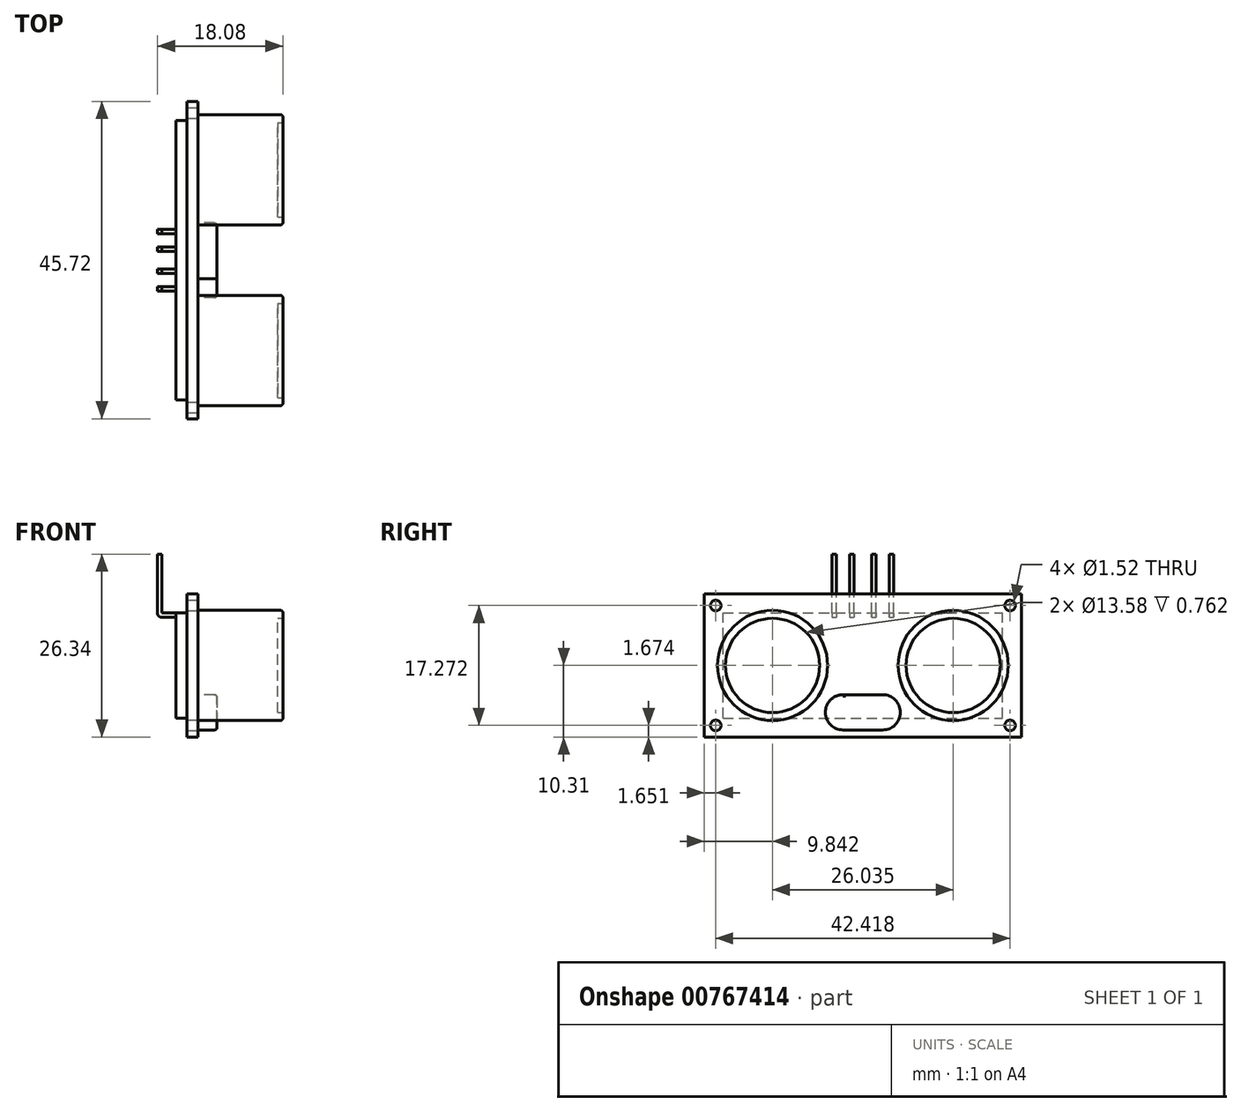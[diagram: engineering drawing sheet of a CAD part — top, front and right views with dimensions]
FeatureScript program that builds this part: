
annotation { "Feature Type Name" : "Feature", "Feature Type Description" : "" }
export const myFeature = defineFeature(function(context is Context, id is Id, definition is map)
    precondition{}
    {
        {
            var Q0;
            Q0=qCreatedBy(makeId("Right.planeOp"),FACE);
            var sketch = newSketch(context, id + "F0", { "sketchPlane" : qUnion([Q0])});
            skLineSegment(sketch, "E0.bottom", {"start": v(22.86, -10.31) * mm, "end": v(-22.86, -10.31) * mm});
            skLineSegment(sketch, "E0.top", {"start": v(22.86, 10.31) * mm, "end": v(-22.86, 10.31) * mm});
            skLineSegment(sketch, "E0.left", {"start": v(22.86, -10.31) * mm, "end": v(22.86, 10.31) * mm});
            skLineSegment(sketch, "E0.right", {"start": v(-22.86, -10.31) * mm, "end": v(-22.86, 10.31) * mm});
            skPoint(sketch, "E0.middle", {"position": v(0, 0) * mm});
            skSolve(sketch);
        }
        {
            var Q0;
            Q0=makeQuery(id+"F0.imprint","IMPRINT",FACE,{"disambiguationData":[TD([[makeQuery(id+"F0.imprint","IMPRINT",EDGE,{"derivedFrom":sQuery(id+"F0.wireOp",EDGE,"E0.bottom")}),-1.0]])]});
            extrude(context, id + "F1", {"entities" : qUnion([Q0]), "oppositeDirection" : true, "depth" : 3.17 * mm});
        }
        {
            var Q0;
            Q0=makeQuery(id+"F1.opExtrude","CAP_FACE",FACE,{"disambiguationData":[OSD([sQuery(id+"F0.wireOp",EDGE,"E0.bottom"),sQuery(id+"F0.wireOp",EDGE,"E0.top"),sQuery(id+"F0.wireOp",EDGE,"E0.left"),sQuery(id+"F0.wireOp",EDGE,"E0.right")])],"isStart":true});
            var sketch = newSketch(context, id + "F2", { "sketchPlane" : qUnion([Q0])});
            skLineSegment(sketch, "E1", {"start": v(0, 0) * mm, "end": v(19.75, 0) * mm, "construction": true});
            skLineSegment(sketch, "E2", {"start": v(0, 0) * mm, "end": v(0, -13.51) * mm, "construction": true});
            skCircle(sketch, "E3", {"center": v(-13.02, 0) * mm, "radius": 7.94 * mm});
            skCircle(sketch, "E4.MirrorC", {"center": v(13.02, 0) * mm, "radius": 7.94 * mm});
            skSolve(sketch);
        }
        {
            var Q0;
            Q0=qSketchRegion(id+"F2",true);
            extrude(context, id + "F3", {"entities" : qUnion([Q0]), "operationType" : NewBodyOperationType.ADD, "depth" : 12.24 * mm});
        }
        {
            var Q0;
            Q0=makeQuery(id+"F1.opExtrude","CAP_FACE",FACE,{"disambiguationData":[OSD([sQuery(id+"F0.wireOp",EDGE,"E0.bottom"),sQuery(id+"F0.wireOp",EDGE,"E0.top"),sQuery(id+"F0.wireOp",EDGE,"E0.left"),sQuery(id+"F0.wireOp",EDGE,"E0.right")])],"isStart":true});
            var sketch = newSketch(context, id + "F4", { "sketchPlane" : qUnion([Q0])});
            skLineSegment(sketch, "E5", {"start": v(0, 0) * mm, "end": v(0, -8.96) * mm, "construction": true});
            skLineSegment(sketch, "E6", {"start": v(0, 0) * mm, "end": v(11, 0) * mm, "construction": true});
            skCircle(sketch, "E7", {"center": v(-21.2, 8.64) * mm, "radius": 0.76 * mm});
            skCircle(sketch, "E8.MirrorC", {"center": v(21.2, 8.64) * mm, "radius": 0.76 * mm});
            skCircle(sketch, "E9.MirrorC", {"center": v(-21.2, -8.64) * mm, "radius": 0.76 * mm});
            skCircle(sketch, "E10.MirrorC", {"center": v(21.2, -8.64) * mm, "radius": 0.76 * mm});
            skSolve(sketch);
        }
        {
            var Q0;
            Q0=qSketchRegion(id+"F4",true);
            extrude(context, id + "F5", {"entities" : qUnion([Q0]), "operationType" : NewBodyOperationType.REMOVE, "oppositeDirection" : true, "depth" : 25.4 * mm});
        }
        {
            var Q0;
            Q0=makeQuery(id+"F1.opExtrude","CAP_FACE",FACE,{"disambiguationData":[OSD([sQuery(id+"F0.wireOp",EDGE,"E0.bottom"),sQuery(id+"F0.wireOp",EDGE,"E0.top"),sQuery(id+"F0.wireOp",EDGE,"E0.left"),sQuery(id+"F0.wireOp",EDGE,"E0.right")])],"isStart":false});
            var sketch = newSketch(context, id + "F6", { "sketchPlane" : qUnion([Q0])});
            skLineSegment(sketch, "E11.bottom", {"start": v(20.15, -7.6) * mm, "end": v(-20.15, -7.6) * mm});
            skLineSegment(sketch, "E11.top", {"start": v(20.15, 7.6) * mm, "end": v(-20.15, 7.6) * mm});
            skLineSegment(sketch, "E11.left", {"start": v(20.15, -7.6) * mm, "end": v(20.15, 7.6) * mm});
            skLineSegment(sketch, "E11.right", {"start": v(-20.15, -7.6) * mm, "end": v(-20.15, 7.6) * mm});
            skPoint(sketch, "E11.middle", {"position": v(0, 0) * mm});
            skLineSegment(sketch, "E12.bottom", {"start": v(25.66, -12.83) * mm, "end": v(-25.66, -12.83) * mm});
            skLineSegment(sketch, "E12.top", {"start": v(25.66, 12.83) * mm, "end": v(-25.66, 12.83) * mm});
            skLineSegment(sketch, "E12.left", {"start": v(25.66, -12.83) * mm, "end": v(25.66, 12.83) * mm});
            skLineSegment(sketch, "E12.right", {"start": v(-25.66, -12.83) * mm, "end": v(-25.66, 12.83) * mm});
            skSolve(sketch);
        }
        {
            var Q0;
            Q0=makeQuery(id+"F6.imprint","IMPRINT",FACE,{"disambiguationData":[TD([[makeQuery(id+"F6.imprint","IMPRINT",EDGE,{"derivedFrom":sQuery(id+"F6.wireOp",EDGE,"E11.bottom")}),1.0]])]});
            var Q1;
            Q1=makeQuery(id+"F6.imprint","IMPRINT",FACE,{"disambiguationData":[TD([[makeQuery(id+"F6.imprint","IMPRINT",EDGE,{"derivedFrom":sQuery(id+"F6.wireOp",EDGE,"E12.bottom")}),-1.0]])]});
            extrude(context, id + "F7", {"entities" : qUnion([Q0, Q1]), "operationType" : NewBodyOperationType.REMOVE, "oppositeDirection" : true, "depth" : 1.57 * mm});
        }
        {
            var Q0;
            Q0=makeQuery(id+"F1.opExtrude","CAP_FACE",FACE,{"disambiguationData":[OSD([sQuery(id+"F0.wireOp",EDGE,"E0.bottom"),sQuery(id+"F0.wireOp",EDGE,"E0.top"),sQuery(id+"F0.wireOp",EDGE,"E0.left"),sQuery(id+"F0.wireOp",EDGE,"E0.right")])],"isStart":true});
            var sketch = newSketch(context, id + "F8", { "sketchPlane" : qUnion([Q0])});
            skLineSegment(sketch, "E13.bottom", {"start": v(-2.69, -4.22) * mm, "end": v(2.86, -4.22) * mm});
            skLineSegment(sketch, "E13.top", {"start": v(-2.85, -9.3) * mm, "end": v(2.88, -9.3) * mm});
            skLineSegment(sketch, "E13.left", {"start": v(-5.4, -6.75) * mm, "end": v(-5.4, -6.76) * mm});
            skPoint(sketch, "E13.middle", {"position": v(0, -6.76) * mm});
            skPoint(sketch, "E14.first.point", {"position": v(2.88, -9.3) * mm});
            skPoint(sketch, "E14.second.point", {"position": v(5.4, -6.76) * mm});
            skPoint(sketch, "E14.third.point", {"position": v(3.38, -4.22) * mm});
            skArc(sketch, "E15", {"start": v(-2.69, -4.22) * mm, "mid": v(-5.4, -6.67) * mm, "end": v(-2.85, -9.3) * mm});
            skPoint(sketch, "E15.first.point", {"position": v(-2.85, -9.3) * mm});
            skPoint(sketch, "E15.second.point", {"position": v(-5.4, -6.76) * mm});
            skPoint(sketch, "E15.third.point", {"position": v(-2.69, -4.22) * mm});
            skArc(sketch, "E16", {"start": v(2.86, -9.3) * mm, "mid": v(5.4, -6.76) * mm, "end": v(2.86, -4.22) * mm});
            skPoint(sketch, "E16.first.point", {"position": v(2.86, -9.3) * mm});
            skPoint(sketch, "E16.second.point", {"position": v(2.86, -4.22) * mm});
            skPoint(sketch, "E17.first.point", {"position": v(3.53, -9.3) * mm});
            skPoint(sketch, "E17.second.point", {"position": v(5.4, -5.54) * mm});
            skPoint(sketch, "E17.third.point", {"position": v(4.54, -4.22) * mm});
            skPoint(sketch, "E18.orphan", {"position": v(5.4, -9.3) * mm});
            skPoint(sketch, "E19.orphan", {"position": v(5.4, -4.22) * mm});
            skPoint(sketch, "E20.orphan", {"position": v(-5.4, -4.22) * mm});
            skPoint(sketch, "E21.orphan", {"position": v(-5.4, -9.3) * mm});
            skSolve(sketch);
        }
        {
            var Q0;
            {var subQ3=sQuery(id+"F8.wireOp",EDGE,"E13.bottom");Q0=makeQuery(id+"F8.imprint","IMPRINT",FACE,{"disambiguationData":[TD([[makeQuery(id+"F8.imprint","IMPRINT",EDGE,{"derivedFrom":subQ3}),-1.0]])]});}
            extrude(context, id + "F9", {"entities" : qUnion([Q0]), "operationType" : NewBodyOperationType.ADD, "depth" : 2.74 * mm});
        }
        {
            var Q0;
            Q0=qCreatedBy(makeId("Front.planeOp"),FACE);
            cPlane(context, id + "F10", {"entities" : qUnion([Q0]), "cplaneType" : CPlaneType.OFFSET, "offset" : 1.27 * mm, "width" : 152.4 * mm, "height" : 152.4 * mm});
        }
        {
            var Q0;
            Q0=qCreatedBy(id+"F10.planeOp",FACE);
            var sketch = newSketch(context, id + "F11", { "sketchPlane" : qUnion([Q0])});
            skLineSegment(sketch, "E22", {"start": v(-1.89, 6.96) * mm, "end": v(-5.29, 6.96) * mm});
            skLineSegment(sketch, "E23", {"start": v(-5.84, 7.51) * mm, "end": v(-5.84, 16.03) * mm});
            skPoint(sketch, "E24.visualSharp", {"position": v(-5.84, 6.96) * mm});
            skArc(sketch, "E24.filletArc", {"start": v(-5.84, 7.51) * mm, "mid": v(-5.68, 7.12) * mm, "end": v(-5.29, 6.96) * mm});
            skLineSegment(sketch, "E25.0", {"start": v(-1.89, 7.57) * mm, "end": v(-5.23, 7.57) * mm});
            skLineSegment(sketch, "E26.0", {"start": v(-5.23, 7.57) * mm, "end": v(-5.23, 16.03) * mm});
            skLineSegment(sketch, "E27", {"start": v(-5.84, 16.03) * mm, "end": v(-5.23, 16.03) * mm});
            skLineSegment(sketch, "E28", {"start": v(-1.89, 7.57) * mm, "end": v(-1.89, 6.96) * mm});
            skSolve(sketch);
        }
        {
            var Q0;
            Q0=makeQuery(id+"F11.imprint","IMPRINT",FACE,{"disambiguationData":[TD([[makeQuery(id+"F11.imprint","IMPRINT",EDGE,{"derivedFrom":sQuery(id+"F11.wireOp",EDGE,"E22")}),-1.0]])]});
            extrude(context, id + "F12", {"entities" : qUnion([Q0]), "depth" : 0.64 * mm});
        }
        {
            var Q0;
            Q0=makeQuery(id+"F12.opExtrude","SWEPT_BODY",BODY,{"disambiguationData":[OSD([sQuery(id+"F11.wireOp",EDGE,"E22"),sQuery(id+"F11.wireOp",EDGE,"E23"),sQuery(id+"F11.wireOp",EDGE,"E24.filletArc"),sQuery(id+"F11.wireOp",EDGE,"E25.0"),sQuery(id+"F11.wireOp",EDGE,"E26.0"),sQuery(id+"F11.wireOp",EDGE,"E27"),sQuery(id+"F11.wireOp",EDGE,"E28")])]});
            transform(context, id + "F13", {"entities" : qUnion([Q0]), "transformType" : TransformType.TRANSLATION_3D, "dx" : 0 * mm, "dy" : -2.54 * mm, "dz" : 0 * mm, "makeCopy" : true});
        }
        {
            var Q0;
            Q0=makeQuery(id+"F13.opPattern","COPY",BODY,{"derivedFrom":makeQuery(id+"F12.opExtrude","SWEPT_BODY",BODY,{"disambiguationData":[OSD([sQuery(id+"F11.wireOp",EDGE,"E22"),sQuery(id+"F11.wireOp",EDGE,"E23"),sQuery(id+"F11.wireOp",EDGE,"E24.filletArc"),sQuery(id+"F11.wireOp",EDGE,"E25.0"),sQuery(id+"F11.wireOp",EDGE,"E26.0"),sQuery(id+"F11.wireOp",EDGE,"E27"),sQuery(id+"F11.wireOp",EDGE,"E28")])]}),"instanceName":"1"});
            var Q1;
            Q1=makeQuery(id+"F12.opExtrude","SWEPT_BODY",BODY,{"disambiguationData":[OSD([sQuery(id+"F11.wireOp",EDGE,"E22"),sQuery(id+"F11.wireOp",EDGE,"E23"),sQuery(id+"F11.wireOp",EDGE,"E24.filletArc"),sQuery(id+"F11.wireOp",EDGE,"E25.0"),sQuery(id+"F11.wireOp",EDGE,"E26.0"),sQuery(id+"F11.wireOp",EDGE,"E27"),sQuery(id+"F11.wireOp",EDGE,"E28")])]});
            var Q2;
            Q2=qCreatedBy(makeId("Front.planeOp"),FACE);
            mirror(context, id + "F14", {"operationType" : NewBodyOperationType.ADD, "entities" : qUnion([Q0, Q1]), "mirrorPlane" : qUnion([Q2])});
        }
        {
            var Q0;
            Q0=makeQuery(id+"F9.opExtrude","CAP_EDGE",EDGE,{"disambiguationData":[OSD([sQuery(id+"F8.wireOp",EDGE,"E16")])],"isStart":false});
            var Q1;
            Q1=makeQuery(id+"F3.opExtrude","CAP_EDGE",EDGE,{"disambiguationData":[OSD([sQuery(id+"F2.wireOp",EDGE,"E3")])],"isStart":false});
            var Q2;
            Q2=makeQuery(id+"F3.opExtrude","CAP_EDGE",EDGE,{"disambiguationData":[OSD([sQuery(id+"F2.wireOp",EDGE,"E4.MirrorC")])],"isStart":false});
            fillet(context, id + "F15", {"entities" : qUnion([Q0, Q1, Q2]), "radius" : 0.38 * mm, "tangentPropagation" : true, "allowEdgeOverflow" : false});
        }
        {
            var Q0;
            Q0=makeQuery(id+"F3.opExtrude","CAP_FACE",FACE,{"disambiguationData":[OSD([sQuery(id+"F2.wireOp",EDGE,"E4.MirrorC")])],"isStart":false});
            var sketch = newSketch(context, id + "F16", { "sketchPlane" : qUnion([Q0])});
            skCircle(sketch, "E29", {"center": v(13.02, 0) * mm, "radius": 6.8 * mm});
            skLineSegment(sketch, "E30", {"start": v(0, 0) * mm, "end": v(0, 5.94) * mm, "construction": true});
            skCircle(sketch, "E31.MirrorC", {"center": v(-13.02, 0) * mm, "radius": 6.8 * mm});
            skSolve(sketch);
        }
        {
            var Q0;
            Q0=qSketchRegion(id+"F16",true);
            extrude(context, id + "F17", {"entities" : qUnion([Q0]), "operationType" : NewBodyOperationType.REMOVE, "oppositeDirection" : true, "depth" : 0.76 * mm});
        }
    });
